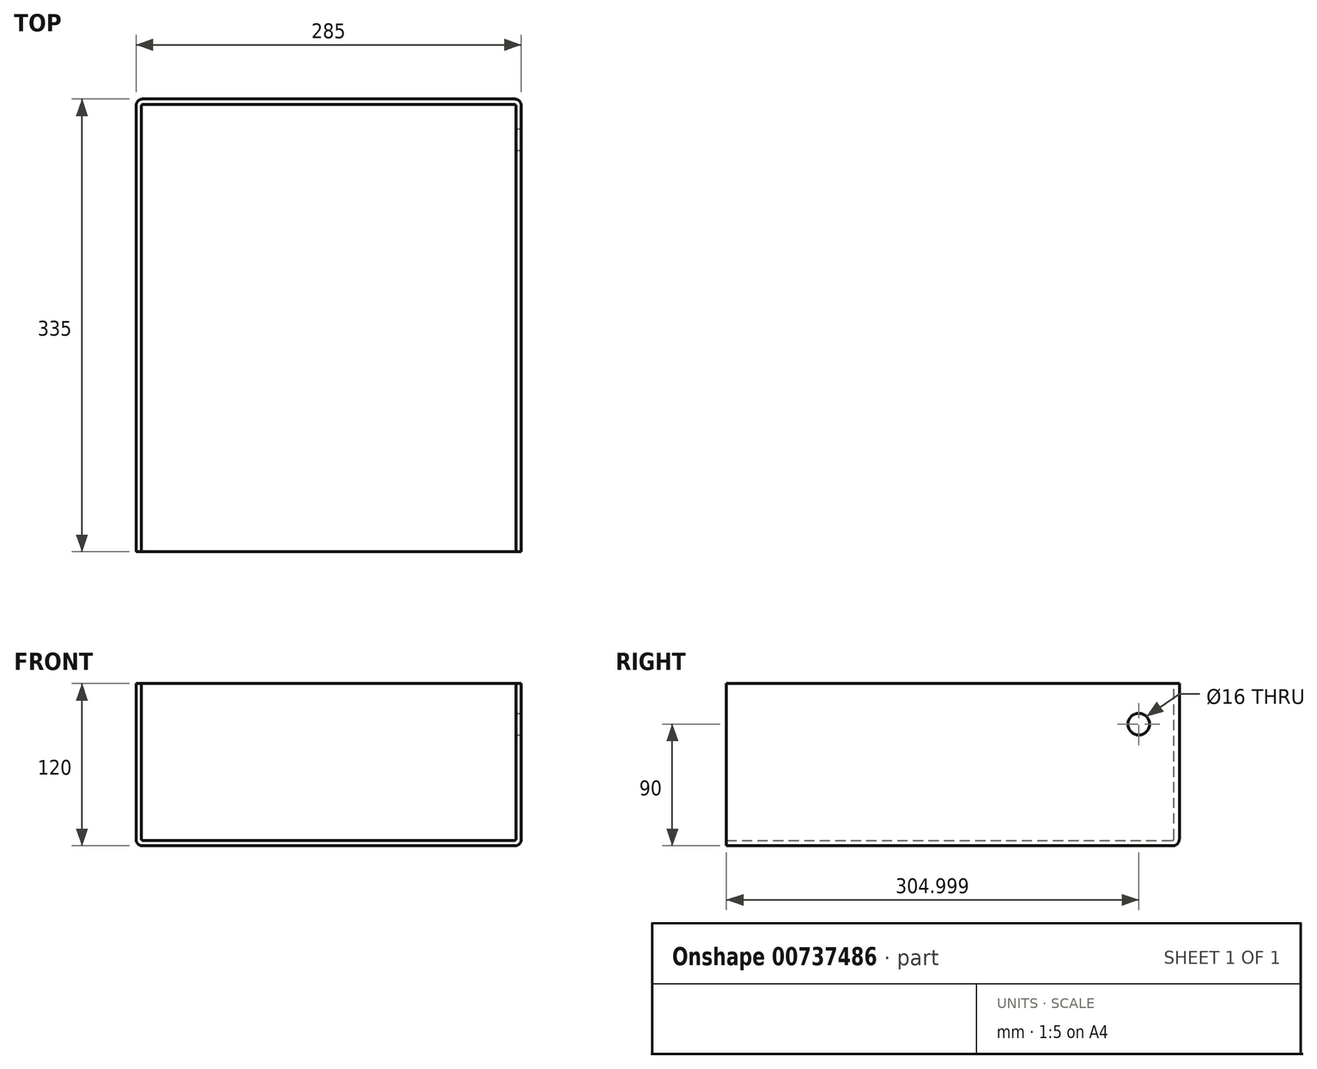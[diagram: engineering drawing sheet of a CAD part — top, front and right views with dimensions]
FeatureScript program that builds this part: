
annotation { "Feature Type Name" : "Feature", "Feature Type Description" : "" }
export const myFeature = defineFeature(function(context is Context, id is Id, definition is map)
    precondition{}
    {
        {
            var Q0;
            Q0=qCreatedBy(makeId("Top.planeOp"),FACE);
            var sketch = newSketch(context, id + "F0", { "sketchPlane" : qUnion([Q0])});
            skLineSegment(sketch, "E0.bottom", {"start": v(-223.23, 281.82) * mm, "end": v(61.77, 281.82) * mm});
            skLineSegment(sketch, "E0.top", {"start": v(-223.23, -53.18) * mm, "end": v(61.77, -53.18) * mm});
            skLineSegment(sketch, "E0.left", {"start": v(-223.23, 281.82) * mm, "end": v(-223.23, -53.18) * mm});
            skLineSegment(sketch, "E0.right", {"start": v(61.77, 281.82) * mm, "end": v(61.77, -53.18) * mm});
            skSolve(sketch);
        }
        {
            var Q0;
            Q0=makeQuery(id+"F0.imprint","IMPRINT",FACE,{"disambiguationData":[TD([[makeQuery(id+"F0.imprint","IMPRINT",EDGE,{"derivedFrom":sQuery(id+"F0.wireOp",EDGE,"E0.bottom")}),-1.0]])]});
            extrude(context, id + "F1", {"entities" : qUnion([Q0]), "depth" : 120 * mm, "offsetDistance" : 25 * mm});
        }
        {
            var Q0;
            Q0=makeQuery(id+"F1.opExtrude","CAP_EDGE",EDGE,{"disambiguationData":[OSD([sQuery(id+"F0.wireOp",EDGE,"E0.left")])],"isStart":true});
            var Q1;
            Q1=makeQuery(id+"F1.opExtrude","CAP_EDGE",EDGE,{"disambiguationData":[OSD([sQuery(id+"F0.wireOp",EDGE,"E0.bottom")])],"isStart":true});
            var Q2;
            Q2=makeQuery(id+"F1.opExtrude","CAP_EDGE",EDGE,{"disambiguationData":[OSD([sQuery(id+"F0.wireOp",EDGE,"E0.right")])],"isStart":true});
            var Q3;
            Q3=makeQuery(id+"F1.opExtrude","SWEPT_EDGE",EDGE,{"disambiguationData":[OSD([sQuery(id+"F0.wireOp",EDGE,"E0.bottom"),sQuery(id+"F0.wireOp",EDGE,"E0.left")])]});
            var Q4;
            Q4=makeQuery(id+"F1.opExtrude","SWEPT_EDGE",EDGE,{"disambiguationData":[OSD([sQuery(id+"F0.wireOp",EDGE,"E0.bottom"),sQuery(id+"F0.wireOp",EDGE,"E0.right")])]});
            fillet(context, id + "F2", {"entities" : qUnion([Q0, Q1, Q2, Q3, Q4]), "radius" : 5 * mm, "tangentPropagation" : true, "allowEdgeOverflow" : false});
        }
        {
            var Q0;
            Q0=makeQuery(id+"F1.opExtrude","CAP_FACE",FACE,{"disambiguationData":[OSD([sQuery(id+"F0.wireOp",EDGE,"E0.bottom"),sQuery(id+"F0.wireOp",EDGE,"E0.top"),sQuery(id+"F0.wireOp",EDGE,"E0.left"),sQuery(id+"F0.wireOp",EDGE,"E0.right")])],"isStart":false});
            var Q1;
            Q1=makeQuery(id+"F1.opExtrude","SWEPT_FACE",FACE,{"disambiguationData":[OSD([sQuery(id+"F0.wireOp",EDGE,"E0.top")])]});
            shell(context, id + "F3", {"entities" : qUnion([Q0, Q1]), "thickness" : 4 * mm});
        }
        {
            var Q0;
            Q0=makeQuery(id+"F1.opExtrude","SWEPT_FACE",FACE,{"disambiguationData":[OSD([sQuery(id+"F0.wireOp",EDGE,"E0.right")])]});
            var sketch = newSketch(context, id + "F4", { "sketchPlane" : qUnion([Q0])});
            skCircle(sketch, "E1", {"center": v(251.82, 90) * mm, "radius": 8 * mm});
            skSolve(sketch);
        }
        {
            var Q0;
            Q0=sQuery(id+"F4.wireOp",VERTEX,"E1.center");
            var Q1;
            Q1=makeQuery(id+"F1.opExtrude","SWEPT_BODY",BODY,{"disambiguationData":[OSD([sQuery(id+"F0.wireOp",EDGE,"E0.bottom"),sQuery(id+"F0.wireOp",EDGE,"E0.top"),sQuery(id+"F0.wireOp",EDGE,"E0.left"),sQuery(id+"F0.wireOp",EDGE,"E0.right")])]});
            hole(context, id + "F5", {"style" : HoleStyle.SIMPLE, "endStyle" : HoleEndStyle.BLIND, "holeDiameter" : 16 * mm, "majorDiameter" : 5 * mm, "holeDepth" : 10 * mm, "isTappedThrough" : true, "tappedDepth" : 12 * mm, "tapClearance" : 3, "locations" : qUnion([Q0]), "scope" : qUnion([Q1])});
        }
    });
